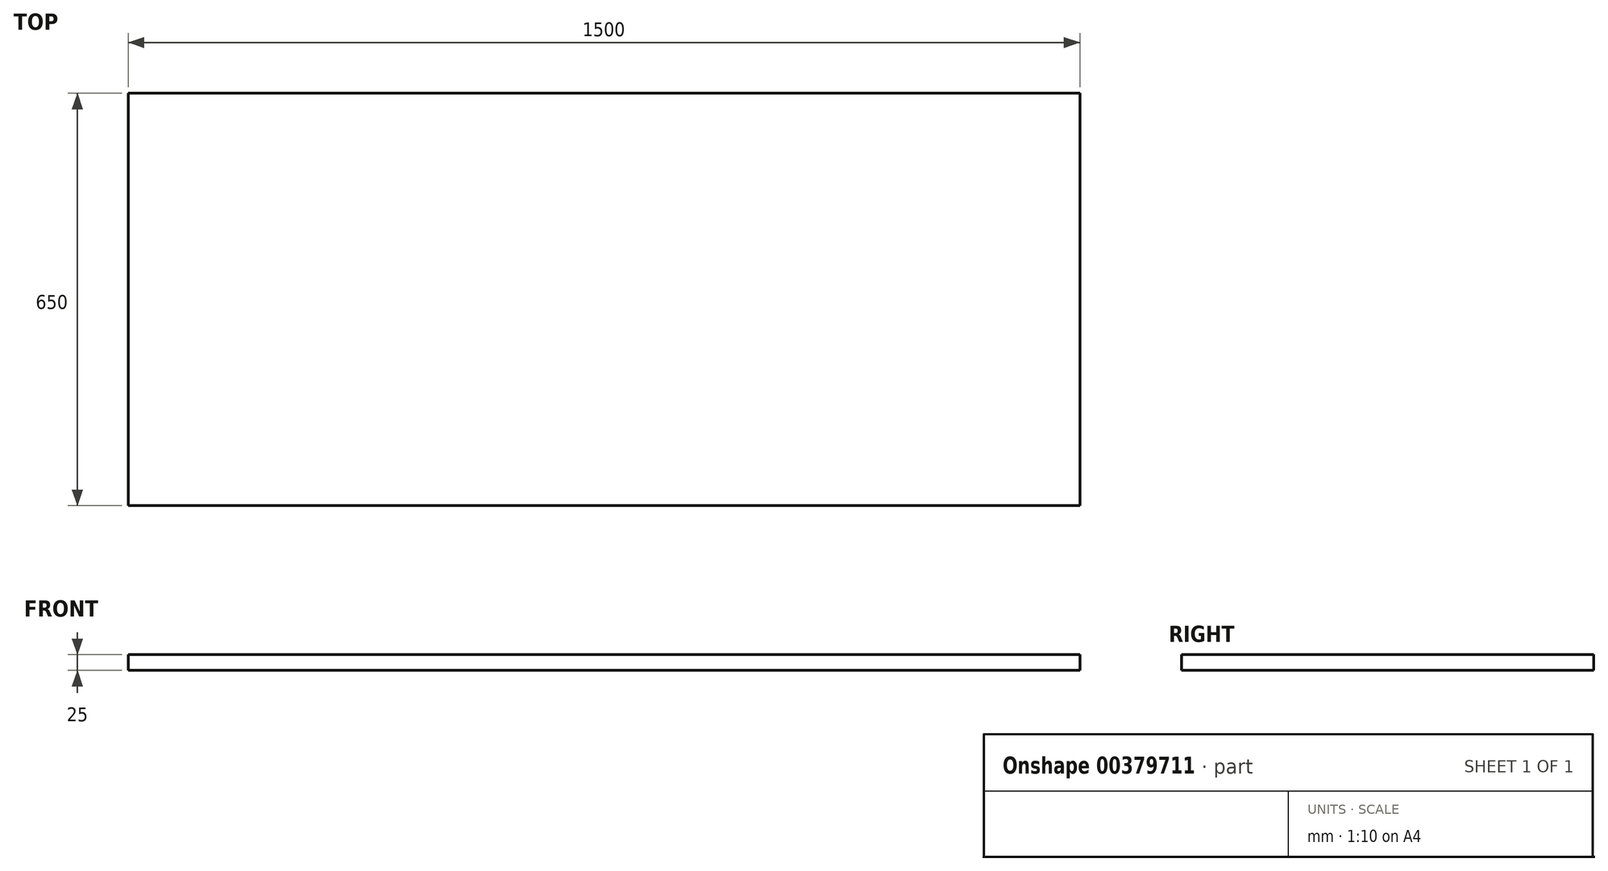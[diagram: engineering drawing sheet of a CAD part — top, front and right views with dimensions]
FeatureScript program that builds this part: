
annotation { "Feature Type Name" : "Feature", "Feature Type Description" : "" }
export const myFeature = defineFeature(function(context is Context, id is Id, definition is map)
    precondition{}
    {
        {
            var Q0;
            Q0=qCreatedBy(makeId("Top.planeOp"),FACE);
            var sketch = newSketch(context, id + "F0", { "sketchPlane" : qUnion([Q0])});
            skLineSegment(sketch, "E0.bottom", {"start": v(-80.84, 625.36) * mm, "end": v(1419.16, 625.36) * mm});
            skLineSegment(sketch, "E0.top", {"start": v(-80.84, -24.64) * mm, "end": v(1419.16, -24.64) * mm});
            skLineSegment(sketch, "E0.left", {"start": v(-80.84, 625.36) * mm, "end": v(-80.84, -24.64) * mm});
            skLineSegment(sketch, "E0.right", {"start": v(1419.16, 625.36) * mm, "end": v(1419.16, -24.64) * mm});
            skSolve(sketch);
        }
        {
            var Q0;
            Q0=makeQuery(id+"F0.imprint","IMPRINT",FACE,{"disambiguationData":[TD([[makeQuery(id+"F0.imprint","IMPRINT",EDGE,{"derivedFrom":sQuery(id+"F0.wireOp",EDGE,"E0.bottom")}),-1.0]])]});
            extrude(context, id + "F1", {"entities" : qUnion([Q0]), "depth" : 25 * mm});
        }
    });
